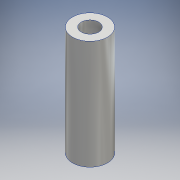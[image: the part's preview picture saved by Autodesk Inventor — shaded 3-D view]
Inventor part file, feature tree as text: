
AUTODESK INVENTOR PART (.ipt)
format: ipt  version: 2016 (Build 200138000, 138)  size: 108,032 bytes
history: native  units: mm
features: sketch x2, extrude x2, hole x2, other x1
ambient origin geometry x8: Origin, YZ Plane, XZ Plane, XY Plane, X Axis, Y Axis, Z Axis, Center Point
bodies: Body1 (feature_tree)
feature tree (7):
  other  "ソリッド1"
  sketch  "スケッチ1"
  extrude  "押し出し1"  Depth=8.0mm
  sketch  "スケッチ2"
  extrude  "押し出し2"  Depth=4.001mm
  hole  "穴1"  [1 undecoded]
  hole  "穴2"  [1 undecoded]
note: 2 required parameter values undecoded (feature->parameter linkage not recoverable at this tier; creation-order binding heuristic only, values carry confidence <= 0.55)
